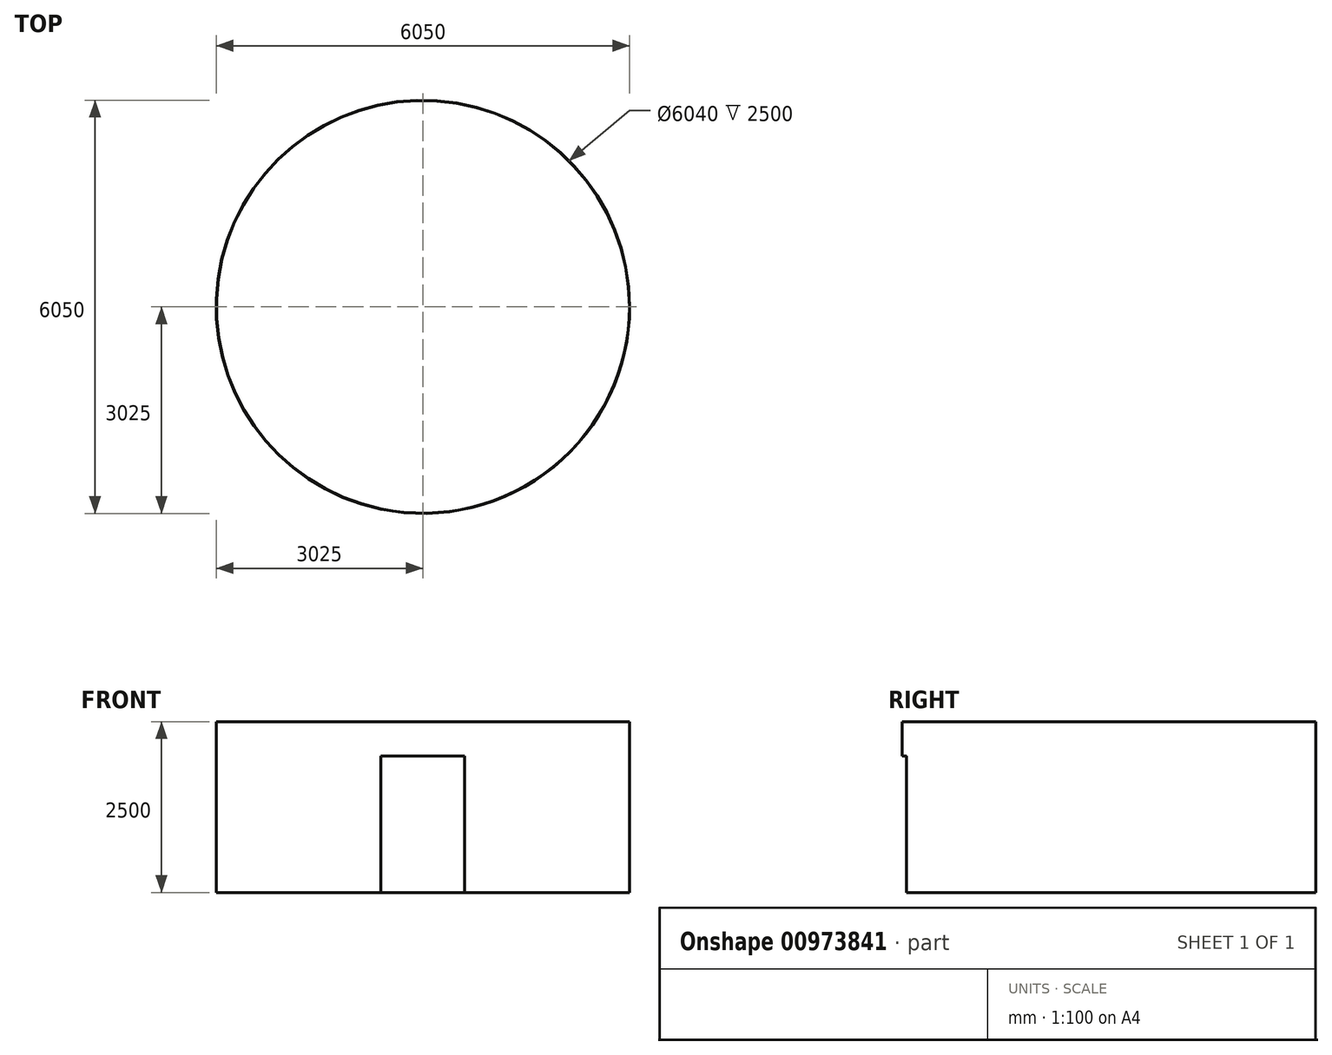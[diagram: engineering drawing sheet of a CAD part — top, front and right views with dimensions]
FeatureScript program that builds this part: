
annotation { "Feature Type Name" : "Feature", "Feature Type Description" : "" }
export const myFeature = defineFeature(function(context is Context, id is Id, definition is map)
    precondition{}
    {
        {
            var Q0;
            Q0=qCreatedBy(makeId("Top.planeOp"),FACE);
            var sketch = newSketch(context, id + "F0", { "sketchPlane" : qUnion([Q0])});
            skCircle(sketch, "E0", {"center": v(0, 0) * mm, "radius": 3020 * mm});
            skCircle(sketch, "E1.0", {"center": v(0, 0) * mm, "radius": 3000 * mm});
            skCircle(sketch, "E2.0", {"center": v(0, 0) * mm, "radius": 3025 * mm});
            skSolve(sketch);
        }
        {
            var Q0;
            Q0 = qSketchRegion(id + "F0", true);
            extrude(context, id + "F1", {"entities" : qUnion([Q0]), "depth" : 2500 * mm, "offsetDistance" : 25 * mm});
        }
        {
            var Q0;
            Q0=qCreatedBy(makeId("Front.planeOp"),FACE);
            var sketch = newSketch(context, id + "F2", { "sketchPlane" : qUnion([Q0])});
            skLineSegment(sketch, "E3.bottom", {"start": v(-612.64, 1999.95) * mm, "end": v(612.64, 1999.95) * mm});
            skLineSegment(sketch, "E3.top", {"start": v(-612.64, 0) * mm, "end": v(612.64, 0) * mm});
            skLineSegment(sketch, "E3.left", {"start": v(-612.64, 1999.95) * mm, "end": v(-612.64, 0) * mm});
            skLineSegment(sketch, "E3.right", {"start": v(612.64, 1999.95) * mm, "end": v(612.64, 0) * mm});
            skPoint(sketch, "E3.middle", {"position": v(0, 0) * mm});
            skSolve(sketch);
        }
        {
            var Q0;
            Q0 = qSketchRegion(id + "F2", true);
            var Q1;
            Q1=makeQuery(id+"F1.opExtrude","SWEPT_FACE",FACE,{"disambiguationData":[OSD([sQuery(id+"F0.wireOp",EDGE,"E2.0")])]});
            extrude(context, id + "F3", {"entities" : qUnion([Q0]), "operationType" : NewBodyOperationType.REMOVE, "endBound" : BoundingType.UP_TO_SURFACE, "depth" : 25 * mm, "endBoundEntityFace" : qUnion([Q1]), "offsetDistance" : 25 * mm});
        }
    });
